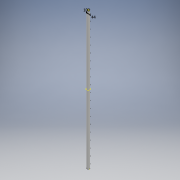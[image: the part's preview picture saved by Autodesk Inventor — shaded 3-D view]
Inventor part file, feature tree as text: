
AUTODESK INVENTOR PART (.ipt)
format: ipt  version: 2017 (Build 210142000, 142)  size: 164,352 bytes
history: native  units: mm
features: extrude x2, sketch x2, pattern_linear x1, projected_geometry x1
ambient origin geometry x8: Origin, YZ Plane, XZ Plane, XY Plane, X Axis, Y Axis, Z Axis, Center Point
bodies: Solid1 (feature_tree)
feature tree (6):
  extrude  "Extrusion1"  Depth=72.0mm
  extrude  "Extrusion2"  Depth=44.0mm
  pattern_linear  "Rectangular Pattern2"  Count1=400 Spacing1=0.0mm
  sketch  "Sketch1"  dims[d0=76.0mm d1=72.0mm]
  sketch  "Sketch2"  dims[d2=2000.0mm d3=0.0mm d4=44.0mm d6=4000.0mm d7=0.0mm d15=2000.0mm d16=0.0mm d23=100.0mm d24=200.0mm d26=200.0mm]
  projected_geometry  "Projected Loop1"
